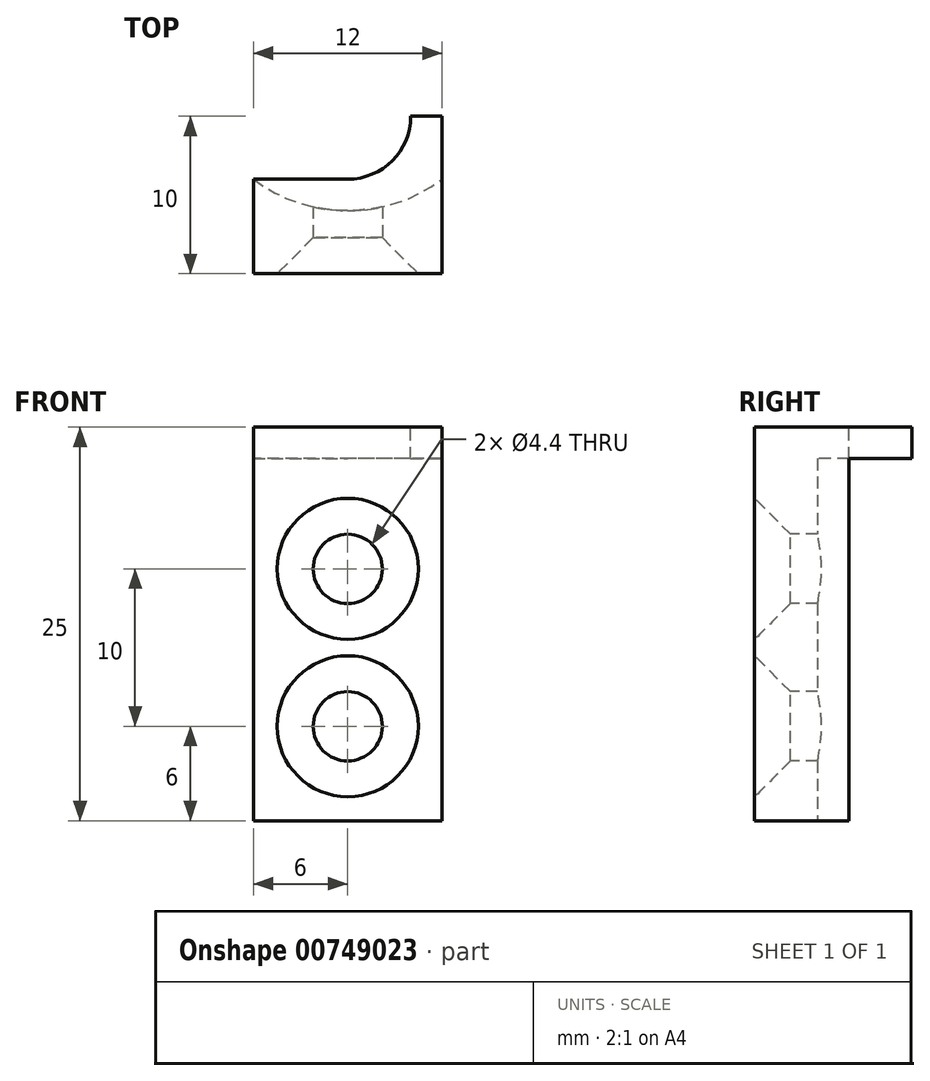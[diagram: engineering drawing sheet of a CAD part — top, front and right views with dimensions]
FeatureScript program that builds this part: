
annotation { "Feature Type Name" : "Feature", "Feature Type Description" : "" }
export const myFeature = defineFeature(function(context is Context, id is Id, definition is map)
    precondition{}
    {
        {
            var Q0;
            Q0=qCreatedBy(makeId("Front.planeOp"),FACE);
            var sketch = newSketch(context, id + "F0", { "sketchPlane" : qUnion([Q0])});
            skLineSegment(sketch, "E0.bottom", {"start": v(0, 0) * mm, "end": v(12, 0) * mm});
            skLineSegment(sketch, "E0.top", {"start": v(0, 25) * mm, "end": v(12, 25) * mm});
            skLineSegment(sketch, "E0.left", {"start": v(0, 0) * mm, "end": v(0, 25) * mm});
            skLineSegment(sketch, "E0.right", {"start": v(12, 0) * mm, "end": v(12, 25) * mm});
            skSolve(sketch);
        }
        {
            var Q0;
            Q0 = qSketchRegion(id + "F0", true);
            extrude(context, id + "F1", {"entities" : qUnion([Q0]), "depth" : 10 * mm, "offsetDistance" : 25 * mm});
        }
        {
            var Q0;
            Q0=makeQuery(id+"F1.opExtrude","SWEPT_FACE",FACE,{"disambiguationData":[OSD([sQuery(id+"F0.wireOp",EDGE,"E0.bottom")])]});
            var sketch = newSketch(context, id + "F2", { "sketchPlane" : qUnion([Q0])});
            skPoint(sketch, "E1", {"position": v(6, -4) * mm});
            skPoint(sketch, "E1.positionSnap0", {"position": v(6, 0) * mm});
            skCircle(sketch, "E2", {"center": v(6, -4) * mm, "radius": 10 * mm});
            skSolve(sketch);
        }
        {
            var Q0;
            Q0 = qSketchRegion(id + "F2", true);
            extrude(context, id + "F3", {"entities" : qUnion([Q0]), "operationType" : NewBodyOperationType.REMOVE, "oppositeDirection" : true, "depth" : 23 * mm, "offsetDistance" : 25 * mm});
        }
        {
            var Q0;
            Q0=makeQuery(id+"F1.opExtrude","SWEPT_FACE",FACE,{"disambiguationData":[OSD([sQuery(id+"F0.wireOp",EDGE,"E0.top")])]});
            var sketch = newSketch(context, id + "F4", { "sketchPlane" : qUnion([Q0])});
            skPoint(sketch, "E3", {"position": v(6, 0) * mm});
            skCircle(sketch, "E4", {"center": v(6, 0) * mm, "radius": 4 * mm});
            skLineSegment(sketch, "E5", {"start": v(6, -4) * mm, "end": v(0, -4) * mm});
            skLineSegment(sketch, "E6", {"start": v(0, -4) * mm, "end": v(0, 0) * mm});
            skSolve(sketch);
        }
        {
            var Q0;
            Q0 = qSketchRegion(id + "F4", true);
            var Q1;
            {var subQ0=sQuery(id+"F4.wireOp",EDGE,"E5");Q1=makeQuery(id+"F4.imprint","IMPRINT",FACE,{"disambiguationData":[TD([[makeQuery(id+"F4.imprint","IMPRINT",EDGE,{"derivedFrom":subQ0}),-1.0]])]});}
            extrude(context, id + "F5", {"entities" : qUnion([Q0, Q1]), "operationType" : NewBodyOperationType.REMOVE, "oppositeDirection" : true, "depth" : 25 * mm, "offsetDistance" : 25 * mm});
        }
        {
            var Q0;
            Q0=makeQuery(id+"F1.opExtrude","CAP_FACE",FACE,{"disambiguationData":[OSD([sQuery(id+"F0.wireOp",EDGE,"E0.bottom"),sQuery(id+"F0.wireOp",EDGE,"E0.top"),sQuery(id+"F0.wireOp",EDGE,"E0.left"),sQuery(id+"F0.wireOp",EDGE,"E0.right")])],"isStart":false});
            var sketch = newSketch(context, id + "F6", { "sketchPlane" : qUnion([Q0])});
            skPoint(sketch, "E7", {"position": v(6, 6) * mm});
            skPoint(sketch, "E7.positionSnap0", {"position": v(6, 0) * mm});
            skPoint(sketch, "E8", {"position": v(6, 16) * mm});
            skSolve(sketch);
        }
        {
            var Q0;
            Q0=sQuery(id+"F6.wireOp",VERTEX,"E7");
            var Q1;
            Q1=sQuery(id+"F6.wireOp",VERTEX,"E8");
            var Q2;
            Q2=makeQuery(id+"F1.opExtrude","SWEPT_BODY",BODY,{"disambiguationData":[OSD([sQuery(id+"F0.wireOp",EDGE,"E0.bottom"),sQuery(id+"F0.wireOp",EDGE,"E0.top"),sQuery(id+"F0.wireOp",EDGE,"E0.left"),sQuery(id+"F0.wireOp",EDGE,"E0.right")])]});
            hole(context, id + "F7", {"style" : HoleStyle.C_SINK, "endStyle" : HoleEndStyle.THROUGH, "standardTappedOrClearance" : lookupTablePath({ "standard" : "ISO", "fit" : "Normal", "size" : "M4", "type" : "Clearance" }), "standardBlindInLast" : lookupTablePath({ "fit" : "Standard", "standard" : "ISO", "size" : "M4", "type" : "Clearance" }), "holeDiameter" : 4.4 * mm, "cSinkDiameter" : 8.96 * mm, "cSinkAngle" : 90 * degree, "majorDiameter" : 5 * mm, "isTappedThrough" : true, "tappedDepth" : 13.25 * mm, "tapClearance" : 3, "locations" : qUnion([Q0, Q1]), "scope" : qUnion([Q2])});
        }
    });
